# Revit family: Q90.195.xxx_with 3 shelves_4+6 drawers
name_source: partatom
category: Möbelsysteme
revit_build: Autodesk Revit 2016 (Build: 20161004_0715(x64)
units: mm (PartAtom-declared; Revit-internal decimal feet)

## family parameters
Arbeitsebenenbasiert = Nein
Beim Laden mit Abzugskörper schneiden = Nein
Bemaßung runder Anschluss = Durchmesser verwenden
Gemeinsam genutzt = Nein
Immer vertikal = Ja
OmniClass-Nummer = 23.40.70.11.11.11.34
OmniClass-Titel = Laboratory Flammables Storage Cabinets
Raumberechnungspunkt = Nein
Teiletyp = Normal

## types (27) — shared parameters
Beschreibung = GS-tested safety storage cabinets for unrestricted storage of flammable hazardous materials in work areas in accordance with EN 14470-1 and TRGS 510 with a fire resistance of 90 (Type 90)
Diff. pressure (Air change 10 times) = 5.0 Pa
Hersteller = asecos GmbH
Price information = Price from fall 2017
Product video = https://www.youtube.com
Sticker position = 13 mm
URL = https://www.asecos.com
cabinet depth = 617 mm
cabinet height = 1968 mm  [stored 6.45669 ft]

## per-type parameters (varying)
- S90.196.060(.WDAS) with 3 shelves, light grey: 1200 mm 3 shelves=Nein; 1200 mm 4 drawers=Nein; 1200 mm 6 drawers=Nein; 600 mm 3 shelves=Ja; 600 mm 4 drawers=Nein; 600 mm 6 drawers=Nein; 600 mm cabinet=Ja; 900 mm 3 shelves=Nein; 900 mm 4 drawers=Nein; 900 mm 6 drawers=Nein; 900/1200 mm cabinet=Nein; Air change 10 times=1.1 L/s; Bestellnummer DACH=30228-001-30249; Distributed load=893.00 kg/m²; Kosten=2300 $; Modell=S90.196.060.WDAS; Order No. Global Markets=30228-001-33659; Price information 2=Prices in EURO, ex works, without taxes and shipping; Typenbild=30227-001.jpg; air duct distance=130 mm  [stored 0.426509 ft]; cabinet colour=RAL 7035 Light grey; cabinet width=597 mm; door width=514 mm  [stored 1.68635 ft]; handle l=500 mm; handle r=507 mm  [stored 1.66339 ft]; handle r visibility=Nein; visibility drill_small=-3 mm; visibility drill_wide=1 mm  [stored 0.00328084 ft]
- S90.196.060(.WDAS) with 4 drawers, light grey: 1200 mm 3 shelves=Nein; 1200 mm 4 drawers=Nein; 1200 mm 6 drawers=Nein; 600 mm 3 shelves=Nein; 600 mm 4 drawers=Ja; 600 mm 6 drawers=Nein; 600 mm cabinet=Ja; 900 mm 3 shelves=Nein; 900 mm 4 drawers=Nein; 900 mm 6 drawers=Nein; 900/1200 mm cabinet=Nein; Air change 10 times=1.1 L/s; Bestellnummer DACH=30228-001-30267; Distributed load=893.00 kg/m²; Kosten=2610 $; Modell=S90.196.060.WDAS; Order No. Global Markets=30228-001-33681; Price information 2=Prices are ex works and without taxes and shipping; Typenbild=30227-001.jpg; air duct distance=130 mm  [stored 0.426509 ft]; cabinet colour=RAL 7035 Light grey; cabinet width=597 mm; door width=514 mm  [stored 1.68635 ft]; handle l=500 mm; handle r=507 mm  [stored 1.66339 ft]; handle r visibility=Nein; visibility drill_small=-3 mm; visibility drill_wide=1 mm  [stored 0.00328084 ft]
- S90.196.060(.WDAS) with 6 drawers, light grey: 1200 mm 3 shelves=Nein; 1200 mm 4 drawers=Nein; 1200 mm 6 drawers=Nein; 600 mm 3 shelves=Nein; 600 mm 4 drawers=Nein; 600 mm 6 drawers=Ja; 600 mm cabinet=Ja; 900 mm 3 shelves=Nein; 900 mm 4 drawers=Nein; 900 mm 6 drawers=Nein; 900/1200 mm cabinet=Nein; Air change 10 times=1.1 L/s; Bestellnummer DACH=30228-001-30269; Distributed load=893.00 kg/m²; Kosten=2850 $; Modell=S90.196.060.WDAS; Order No. Global Markets=30228-001-33683; Price information 2=Prices are ex works and without taxes and shipping; Typenbild=30227-001.jpg; air duct distance=130 mm  [stored 0.426509 ft]; cabinet colour=RAL 7035 Light grey; cabinet width=597 mm; door width=514 mm  [stored 1.68635 ft]; handle l=500 mm; handle r=507 mm  [stored 1.66339 ft]; handle r visibility=Nein; visibility drill_small=-3 mm; visibility drill_wide=1 mm  [stored 0.00328084 ft]
- S90.196.060(.WDAS) with 3 shelves, warning yellow: 1200 mm 3 shelves=Nein; 1200 mm 4 drawers=Nein; 1200 mm 6 drawers=Nein; 600 mm 3 shelves=Ja; 600 mm 4 drawers=Nein; 600 mm 6 drawers=Nein; 600 mm cabinet=Ja; 900 mm 3 shelves=Nein; 900 mm 4 drawers=Nein; 900 mm 6 drawers=Nein; 900/1200 mm cabinet=Nein; Air change 10 times=1.1 L/s; Bestellnummer DACH=30228-002-30249; Distributed load=893.00 kg/m²; Kosten=2300 $; Modell=S90.196.060.WDAS; Order No. Global Markets=30228-002-33659; Price information 2=Prices are ex works and without taxes and shipping; Typenbild=30227-002.jpg; air duct distance=130 mm  [stored 0.426509 ft]; cabinet colour=RAL 1004 Warning yellow; cabinet width=597 mm; door width=514 mm  [stored 1.68635 ft]; handle l=500 mm; handle r=507 mm  [stored 1.66339 ft]; handle r visibility=Nein; visibility drill_small=-3 mm; visibility drill_wide=1 mm  [stored 0.00328084 ft]
- S90.196.060(.WDAS) with 4 drawers, warning yellow: 1200 mm 3 shelves=Nein; 1200 mm 4 drawers=Nein; 1200 mm 6 drawers=Nein; 600 mm 3 shelves=Nein; 600 mm 4 drawers=Ja; 600 mm 6 drawers=Nein; 600 mm cabinet=Ja; 900 mm 3 shelves=Nein; 900 mm 4 drawers=Nein; 900 mm 6 drawers=Nein; 900/1200 mm cabinet=Nein; Air change 10 times=1.1 L/s; Bestellnummer DACH=30228-002-30267; Distributed load=893.00 kg/m²; Kosten=2610 $; Modell=S90.196.060.WDAS; Order No. Global Markets=30228-002-33681; Price information 2=Prices are ex works and without taxes and shipping; Typenbild=30227-002.jpg; air duct distance=130 mm  [stored 0.426509 ft]; cabinet colour=RAL 1004 Warning yellow; cabinet width=597 mm; door width=514 mm  [stored 1.68635 ft]; handle l=500 mm; handle r=507 mm  [stored 1.66339 ft]; handle r visibility=Nein; visibility drill_small=-3 mm; visibility drill_wide=1 mm  [stored 0.00328084 ft]
- S90.196.060(.WDAS) with 6 drawers, warning yellow: 1200 mm 3 shelves=Nein; 1200 mm 4 drawers=Nein; 1200 mm 6 drawers=Nein; 600 mm 3 shelves=Nein; 600 mm 4 drawers=Nein; 600 mm 6 drawers=Ja; 600 mm cabinet=Ja; 900 mm 3 shelves=Nein; 900 mm 4 drawers=Nein; 900 mm 6 drawers=Nein; 900/1200 mm cabinet=Nein; Air change 10 times=1.1 L/s; Bestellnummer DACH=30228-002-30269; Distributed load=893.00 kg/m²; Kosten=2850 $; Modell=S90.196.060.WDAS; Order No. Global Markets=30228-002-33683; Price information 2=Prices are ex works and without taxes and shipping; Typenbild=30227-002.jpg; air duct distance=130 mm  [stored 0.426509 ft]; cabinet colour=RAL 1004 Warning yellow; cabinet width=597 mm; door width=514 mm  [stored 1.68635 ft]; handle l=500 mm; handle r=507 mm  [stored 1.66339 ft]; handle r visibility=Nein; visibility drill_small=-3 mm; visibility drill_wide=1 mm  [stored 0.00328084 ft]
- S90.196.090(.WDAS) with 3 shelves, light grey: 1200 mm 3 shelves=Nein; 1200 mm 4 drawers=Nein; 1200 mm 6 drawers=Nein; 600 mm 3 shelves=Nein; 600 mm 4 drawers=Nein; 600 mm 6 drawers=Nein; 600 mm cabinet=Nein; 900 mm 3 shelves=Ja; 900 mm 4 drawers=Nein; 900 mm 6 drawers=Nein; 900/1200 mm cabinet=Ja; Air change 10 times=1.9 L/s; Bestellnummer DACH=30205-001-30208; Distributed load=628.00 kg/m²; Kosten=2860 $; Modell=S90.196.090.WDAS; Order No. Global Markets=30205-001-33705; Price information 2=Prices are ex works and without taxes and shipping; Typenbild=30204-001.jpg; air duct distance=115 mm  [stored 0.377297 ft]; cabinet colour=RAL 7035 Light grey; cabinet width=897 mm; door width=403 mm; handle l=389 mm; handle r=507 mm  [stored 1.66339 ft]; handle r visibility=Ja; visibility drill_small=1 mm  [stored 0.00328084 ft]; visibility drill_wide=-3 mm
- S90.196.090(.WDAS) with 4 drawers, light grey: 1200 mm 3 shelves=Nein; 1200 mm 4 drawers=Nein; 1200 mm 6 drawers=Nein; 600 mm 3 shelves=Nein; 600 mm 4 drawers=Nein; 600 mm 6 drawers=Nein; 600 mm cabinet=Nein; 900 mm 3 shelves=Nein; 900 mm 4 drawers=Ja; 900 mm 6 drawers=Nein; 900/1200 mm cabinet=Ja; Air change 10 times=1.9 L/s; Bestellnummer DACH=30205-001-30218; Distributed load=628.00 kg/m²; Kosten=3420 $; Modell=S90.196.090.WDAS; Order No. Global Markets=30205-001-33709; Price information 2=Prices are ex works and without taxes and shipping; Typenbild=30204-001.jpg; air duct distance=115 mm  [stored 0.377297 ft]; cabinet colour=RAL 7035 Light grey; cabinet width=897 mm; door width=403 mm; handle l=389 mm; handle r=507 mm  [stored 1.66339 ft]; handle r visibility=Ja; visibility drill_small=1 mm  [stored 0.00328084 ft]; visibility drill_wide=-3 mm
- S90.196.090(.WDAS) with 6 drawers, light grey: 1200 mm 3 shelves=Nein; 1200 mm 4 drawers=Nein; 1200 mm 6 drawers=Nein; 600 mm 3 shelves=Nein; 600 mm 4 drawers=Nein; 600 mm 6 drawers=Nein; 600 mm cabinet=Nein; 900 mm 3 shelves=Nein; 900 mm 4 drawers=Nein; 900 mm 6 drawers=Ja; 900/1200 mm cabinet=Ja; Air change 10 times=1.9 L/s; Bestellnummer DACH=30205-001-30220; Distributed load=628.00 kg/m²; Kosten=3800 $; Modell=S90.196.090.WDAS; Order No. Global Markets=30205-001-33711; Price information 2=Prices are ex works and without taxes and shipping; Typenbild=30204-001.jpg; air duct distance=115 mm  [stored 0.377297 ft]; cabinet colour=RAL 7035 Light grey; cabinet width=897 mm; door width=403 mm; handle l=389 mm; handle r=507 mm  [stored 1.66339 ft]; handle r visibility=Ja; visibility drill_small=1 mm  [stored 0.00328084 ft]; visibility drill_wide=-3 mm
- S90.196.090(.WDAS) with 3 shelves, warning yellow: 1200 mm 3 shelves=Nein; 1200 mm 4 drawers=Nein; 1200 mm 6 drawers=Nein; 600 mm 3 shelves=Nein; 600 mm 4 drawers=Nein; 600 mm 6 drawers=Nein; 600 mm cabinet=Nein; 900 mm 3 shelves=Ja; 900 mm 4 drawers=Nein; 900 mm 6 drawers=Nein; 900/1200 mm cabinet=Ja; Air change 10 times=1.9 L/s; Bestellnummer DACH=30205-002-30208; Distributed load=628.00 kg/m²; Kosten=2860 $; Modell=S90.196.090.WDAS; Order No. Global Markets=30205-002-33705; Price information 2=Prices are ex works and without taxes and shipping; Typenbild=30204-002.jpg; air duct distance=115 mm  [stored 0.377297 ft]; cabinet colour=RAL 1004 Warning yellow; cabinet width=897 mm; door width=403 mm; handle l=389 mm; handle r=507 mm  [stored 1.66339 ft]; handle r visibility=Ja; visibility drill_small=1 mm  [stored 0.00328084 ft]; visibility drill_wide=-3 mm
- S90.196.090(.WDAS) with 4 drawers, warning yellow: 1200 mm 3 shelves=Nein; 1200 mm 4 drawers=Nein; 1200 mm 6 drawers=Nein; 600 mm 3 shelves=Nein; 600 mm 4 drawers=Nein; 600 mm 6 drawers=Nein; 600 mm cabinet=Nein; 900 mm 3 shelves=Nein; 900 mm 4 drawers=Ja; 900 mm 6 drawers=Nein; 900/1200 mm cabinet=Ja; Air change 10 times=1.9 L/s; Bestellnummer DACH=30205-002-30218; Distributed load=628.00 kg/m²; Kosten=3420 $; Modell=S90.196.090.WDAS; Order No. Global Markets=30205-002-33709; Price information 2=Prices are ex works and without taxes and shipping; Typenbild=30204-002.jpg; air duct distance=115 mm  [stored 0.377297 ft]; cabinet colour=RAL 1004 Warning yellow; cabinet width=897 mm; door width=403 mm; handle l=389 mm; handle r=507 mm  [stored 1.66339 ft]; handle r visibility=Ja; visibility drill_small=1 mm  [stored 0.00328084 ft]; visibility drill_wide=-3 mm
- S90.196.090(.WDAS) with 6 drawers, warning yellow: 1200 mm 3 shelves=Nein; 1200 mm 4 drawers=Nein; 1200 mm 6 drawers=Nein; 600 mm 3 shelves=Nein; 600 mm 4 drawers=Nein; 600 mm 6 drawers=Nein; 600 mm cabinet=Nein; 900 mm 3 shelves=Nein; 900 mm 4 drawers=Nein; 900 mm 6 drawers=Ja; 900/1200 mm cabinet=Ja; Air change 10 times=1.9 L/s; Bestellnummer DACH=30205-002-30220; Distributed load=628.00 kg/m²; Kosten=3800 $; Modell=S90.196.090.WDAS; Order No. Global Markets=30205-002-33711; Price information 2=Prices are ex works and without taxes and shipping; Typenbild=30204-002.jpg; air duct distance=115 mm  [stored 0.377297 ft]; cabinet colour=RAL 1004 Warning yellow; cabinet width=897 mm; door width=403 mm; handle l=389 mm; handle r=507 mm  [stored 1.66339 ft]; handle r visibility=Ja; visibility drill_small=1 mm  [stored 0.00328084 ft]; visibility drill_wide=-3 mm
- S90.196.120(.WDAS) with 3 shelves, light grey: 1200 mm 3 shelves=Ja; 1200 mm 4 drawers=Nein; 1200 mm 6 drawers=Nein; 600 mm 3 shelves=Nein; 600 mm 4 drawers=Nein; 600 mm 6 drawers=Nein; 600 mm cabinet=Nein; 900 mm 3 shelves=Nein; 900 mm 4 drawers=Nein; 900 mm 6 drawers=Nein; 900/1200 mm cabinet=Ja; Air change 10 times=2.8 L/s; Bestellnummer DACH=30116-001-30127; Distributed load=528.00 kg/m²; Kosten=2970 $; Modell=S90.196.120.WDAS; Order No. Global Markets=30116-001-33715; Price information 2=Prices are ex works and without taxes and shipping; Typenbild=30115-001.jpg; air duct distance=115 mm  [stored 0.377297 ft]; cabinet colour=RAL 7035 Light grey; cabinet width=1197 mm; door width=553 mm; handle l=538 mm; handle r=658 mm; handle r visibility=Ja; visibility drill_small=1 mm  [stored 0.00328084 ft]; visibility drill_wide=-3 mm
- S90.196.120(.WDAS) with 4 drawers, light grey: 1200 mm 3 shelves=Nein; 1200 mm 4 drawers=Ja; 1200 mm 6 drawers=Nein; 600 mm 3 shelves=Nein; 600 mm 4 drawers=Nein; 600 mm 6 drawers=Nein; 600 mm cabinet=Nein; 900 mm 3 shelves=Nein; 900 mm 4 drawers=Nein; 900 mm 6 drawers=Nein; 900/1200 mm cabinet=Ja; Air change 10 times=2.8 L/s; Bestellnummer DACH=30116-001-30147; Distributed load=528.00 kg/m²; Kosten=3530 $; Modell=S90.196.120.WDAS; Order No. Global Markets=30116-001-33724; Price information 2=Prices are ex works and without taxes and shipping; Typenbild=30115-001.jpg; air duct distance=115 mm  [stored 0.377297 ft]; cabinet colour=RAL 7035 Light grey; cabinet width=1197 mm; door width=553 mm; handle l=538 mm; handle r=658 mm; handle r visibility=Ja; visibility drill_small=1 mm  [stored 0.00328084 ft]; visibility drill_wide=-3 mm
- S90.196.120(.WDAS) with 6 drawers, light grey: 1200 mm 3 shelves=Nein; 1200 mm 4 drawers=Nein; 1200 mm 6 drawers=Ja; 600 mm 3 shelves=Nein; 600 mm 4 drawers=Nein; 600 mm 6 drawers=Nein; 600 mm cabinet=Nein; 900 mm 3 shelves=Nein; 900 mm 4 drawers=Nein; 900 mm 6 drawers=Nein; 900/1200 mm cabinet=Ja; Air change 10 times=2.8 L/s; Bestellnummer DACH=30116-001-30149; Distributed load=528.00 kg/m²; Kosten=3910 $; Modell=S90.196.120.WDAS; Order No. Global Markets=30116-001-33726; Price information 2=Prices are ex works and without taxes and shipping; Typenbild=30115-001.jpg; air duct distance=115 mm  [stored 0.377297 ft]; cabinet colour=RAL 7035 Light grey; cabinet width=1197 mm; door width=553 mm; handle l=538 mm; handle r=658 mm; handle r visibility=Ja; visibility drill_small=1 mm  [stored 0.00328084 ft]; visibility drill_wide=-3 mm
- S90.196.120(.WDAS) with 3 shelves, warning yellow: 1200 mm 3 shelves=Ja; 1200 mm 4 drawers=Nein; 1200 mm 6 drawers=Nein; 600 mm 3 shelves=Nein; 600 mm 4 drawers=Nein; 600 mm 6 drawers=Nein; 600 mm cabinet=Nein; 900 mm 3 shelves=Nein; 900 mm 4 drawers=Nein; 900 mm 6 drawers=Nein; 900/1200 mm cabinet=Ja; Air change 10 times=2.8 L/s; Bestellnummer DACH=30116-002-30127; Distributed load=528.00 kg/m²; Kosten=2970 $; Modell=S90.196.120.WDAS; Order No. Global Markets=30116-002-33715; Price information 2=Prices are ex works and without taxes and shipping; Typenbild=30115-002.jpg; air duct distance=115 mm  [stored 0.377297 ft]; cabinet colour=RAL 1004 Warning yellow; cabinet width=1197 mm; door width=553 mm; handle l=538 mm; handle r=658 mm; handle r visibility=Ja; visibility drill_small=1 mm  [stored 0.00328084 ft]; visibility drill_wide=-3 mm
- S90.196.120(.WDAS) with 4 drawers, warning yellow: 1200 mm 3 shelves=Nein; 1200 mm 4 drawers=Ja; 1200 mm 6 drawers=Nein; 600 mm 3 shelves=Nein; 600 mm 4 drawers=Nein; 600 mm 6 drawers=Nein; 600 mm cabinet=Nein; 900 mm 3 shelves=Nein; 900 mm 4 drawers=Nein; 900 mm 6 drawers=Nein; 900/1200 mm cabinet=Ja; Air change 10 times=2.8 L/s; Bestellnummer DACH=30116-002-30147; Distributed load=528.00 kg/m²; Kosten=3530 $; Modell=S90.196.120.WDAS; Order No. Global Markets=30116-002-33724; Price information 2=Prices are ex works and without taxes and shipping; Typenbild=30115-002.jpg; air duct distance=115 mm  [stored 0.377297 ft]; cabinet colour=RAL 1004 Warning yellow; cabinet width=1197 mm; door width=553 mm; handle l=538 mm; handle r=658 mm; handle r visibility=Ja; visibility drill_small=1 mm  [stored 0.00328084 ft]; visibility drill_wide=-3 mm
- S90.196.120(.WDAS) with 6 drawers, warning yellow: 1200 mm 3 shelves=Nein; 1200 mm 4 drawers=Nein; 1200 mm 6 drawers=Ja; 600 mm 3 shelves=Nein; 600 mm 4 drawers=Nein; 600 mm 6 drawers=Nein; 600 mm cabinet=Nein; 900 mm 3 shelves=Nein; 900 mm 4 drawers=Nein; 900 mm 6 drawers=Nein; 900/1200 mm cabinet=Ja; Air change 10 times=2.8 L/s; Bestellnummer DACH=30116-002-30149; Distributed load=528.00 kg/m²; Kosten=3910 $; Modell=S90.196.120.WDAS; Order No. Global Markets=30116-002-33726; Price information 2=Prices are ex works and without taxes and shipping; Typenbild=30115-002.jpg; air duct distance=115 mm  [stored 0.377297 ft]; cabinet colour=RAL 1004 Warning yellow; cabinet width=1197 mm; door width=553 mm; handle l=538 mm; handle r=658 mm; handle r visibility=Ja; visibility drill_small=1 mm  [stored 0.00328084 ft]; visibility drill_wide=-3 mm
- S90.196.060(.WDAS) with 3 shelves, pure white: 1200 mm 3 shelves=Nein; 1200 mm 4 drawers=Nein; 1200 mm 6 drawers=Nein; 600 mm 3 shelves=Ja; 600 mm 4 drawers=Nein; 600 mm 6 drawers=Nein; 600 mm cabinet=Ja; 900 mm 3 shelves=Nein; 900 mm 4 drawers=Nein; 900 mm 6 drawers=Nein; 900/1200 mm cabinet=Nein; Air change 10 times=1.1 L/s; Bestellnummer DACH=30228-001-30249; Distributed load=893.00 kg/m²; Kosten=2300 $; Modell=S90.196.060.WDAS; Order No. Global Markets=30228-001-33659; Price information 2=Prices in EURO, ex works, without taxes and shipping; Typenbild=30227-001.jpg; air duct distance=130 mm  [stored 0.426509 ft]; cabinet colour=RAL 9010 Pure white; cabinet width=597 mm; door width=514 mm  [stored 1.68635 ft]; handle l=500 mm; handle r=507 mm  [stored 1.66339 ft]; handle r visibility=Nein; visibility drill_small=-3 mm; visibility drill_wide=1 mm  [stored 0.00328084 ft]
- S90.196.060(.WDAS) with 4 drawers, pure white: 1200 mm 3 shelves=Nein; 1200 mm 4 drawers=Nein; 1200 mm 6 drawers=Nein; 600 mm 3 shelves=Nein; 600 mm 4 drawers=Ja; 600 mm 6 drawers=Nein; 600 mm cabinet=Ja; 900 mm 3 shelves=Nein; 900 mm 4 drawers=Nein; 900 mm 6 drawers=Nein; 900/1200 mm cabinet=Nein; Air change 10 times=1.1 L/s; Bestellnummer DACH=30228-001-30267; Distributed load=893.00 kg/m²; Kosten=2610 $; Modell=S90.196.060.WDAS; Order No. Global Markets=30228-001-33681; Price information 2=Prices are ex works and without taxes and shipping; Typenbild=30227-001.jpg; air duct distance=130 mm  [stored 0.426509 ft]; cabinet colour=RAL 9010 Pure white; cabinet width=597 mm; door width=514 mm  [stored 1.68635 ft]; handle l=500 mm; handle r=507 mm  [stored 1.66339 ft]; handle r visibility=Nein; visibility drill_small=-3 mm; visibility drill_wide=1 mm  [stored 0.00328084 ft]
- S90.196.060(.WDAS) with 6 drawers, pure white: 1200 mm 3 shelves=Nein; 1200 mm 4 drawers=Nein; 1200 mm 6 drawers=Nein; 600 mm 3 shelves=Nein; 600 mm 4 drawers=Nein; 600 mm 6 drawers=Ja; 600 mm cabinet=Ja; 900 mm 3 shelves=Nein; 900 mm 4 drawers=Nein; 900 mm 6 drawers=Nein; 900/1200 mm cabinet=Nein; Air change 10 times=1.1 L/s; Bestellnummer DACH=30228-001-30269; Distributed load=893.00 kg/m²; Kosten=2850 $; Modell=S90.196.060.WDAS; Order No. Global Markets=30228-001-33683; Price information 2=Prices are ex works and without taxes and shipping; Typenbild=30227-001.jpg; air duct distance=130 mm  [stored 0.426509 ft]; cabinet colour=RAL 9010 Pure white; cabinet width=597 mm; door width=514 mm  [stored 1.68635 ft]; handle l=500 mm; handle r=507 mm  [stored 1.66339 ft]; handle r visibility=Nein; visibility drill_small=-3 mm; visibility drill_wide=1 mm  [stored 0.00328084 ft]
- S90.196.090(.WDAS) with 3 shelves, pure white: 1200 mm 3 shelves=Nein; 1200 mm 4 drawers=Nein; 1200 mm 6 drawers=Nein; 600 mm 3 shelves=Nein; 600 mm 4 drawers=Nein; 600 mm 6 drawers=Nein; 600 mm cabinet=Nein; 900 mm 3 shelves=Ja; 900 mm 4 drawers=Nein; 900 mm 6 drawers=Nein; 900/1200 mm cabinet=Ja; Air change 10 times=1.9 L/s; Bestellnummer DACH=30205-001-30208; Distributed load=628.00 kg/m²; Kosten=2860 $; Modell=S90.196.090.WDAS; Order No. Global Markets=30205-001-33705; Price information 2=Prices are ex works and without taxes and shipping; Typenbild=30204-001.jpg; air duct distance=115 mm  [stored 0.377297 ft]; cabinet colour=RAL 9010 Pure white; cabinet width=897 mm; door width=403 mm; handle l=389 mm; handle r=507 mm  [stored 1.66339 ft]; handle r visibility=Ja; visibility drill_small=1 mm  [stored 0.00328084 ft]; visibility drill_wide=-3 mm
- S90.196.090(.WDAS) with 4 drawers, pure white: 1200 mm 3 shelves=Nein; 1200 mm 4 drawers=Nein; 1200 mm 6 drawers=Nein; 600 mm 3 shelves=Nein; 600 mm 4 drawers=Nein; 600 mm 6 drawers=Nein; 600 mm cabinet=Nein; 900 mm 3 shelves=Nein; 900 mm 4 drawers=Ja; 900 mm 6 drawers=Nein; 900/1200 mm cabinet=Ja; Air change 10 times=1.9 L/s; Bestellnummer DACH=30205-001-30218; Distributed load=628.00 kg/m²; Kosten=3420 $; Modell=S90.196.090.WDAS; Order No. Global Markets=30205-001-33709; Price information 2=Prices are ex works and without taxes and shipping; Typenbild=30204-001.jpg; air duct distance=115 mm  [stored 0.377297 ft]; cabinet colour=RAL 9010 Pure white; cabinet width=897 mm; door width=403 mm; handle l=389 mm; handle r=507 mm  [stored 1.66339 ft]; handle r visibility=Ja; visibility drill_small=1 mm  [stored 0.00328084 ft]; visibility drill_wide=-3 mm
- S90.196.090(.WDAS) with 6 drawers, pure white: 1200 mm 3 shelves=Nein; 1200 mm 4 drawers=Nein; 1200 mm 6 drawers=Nein; 600 mm 3 shelves=Nein; 600 mm 4 drawers=Nein; 600 mm 6 drawers=Nein; 600 mm cabinet=Nein; 900 mm 3 shelves=Nein; 900 mm 4 drawers=Nein; 900 mm 6 drawers=Ja; 900/1200 mm cabinet=Ja; Air change 10 times=1.9 L/s; Bestellnummer DACH=30205-001-30220; Distributed load=628.00 kg/m²; Kosten=3800 $; Modell=S90.196.090.WDAS; Order No. Global Markets=30205-001-33711; Price information 2=Prices are ex works and without taxes and shipping; Typenbild=30204-001.jpg; air duct distance=115 mm  [stored 0.377297 ft]; cabinet colour=RAL 9010 Pure white; cabinet width=897 mm; door width=403 mm; handle l=389 mm; handle r=507 mm  [stored 1.66339 ft]; handle r visibility=Ja; visibility drill_small=1 mm  [stored 0.00328084 ft]; visibility drill_wide=-3 mm
- S90.196.120(.WDAS) with 3 shelves, pure white: 1200 mm 3 shelves=Ja; 1200 mm 4 drawers=Nein; 1200 mm 6 drawers=Nein; 600 mm 3 shelves=Nein; 600 mm 4 drawers=Nein; 600 mm 6 drawers=Nein; 600 mm cabinet=Nein; 900 mm 3 shelves=Nein; 900 mm 4 drawers=Nein; 900 mm 6 drawers=Nein; 900/1200 mm cabinet=Ja; Air change 10 times=2.8 L/s; Bestellnummer DACH=30116-001-30127; Distributed load=528.00 kg/m²; Kosten=2970 $; Modell=S90.196.120.WDAS; Order No. Global Markets=30116-001-33715; Price information 2=Prices are ex works and without taxes and shipping; Typenbild=30115-001.jpg; air duct distance=115 mm  [stored 0.377297 ft]; cabinet colour=RAL 9010 Pure white; cabinet width=1197 mm; door width=553 mm; handle l=538 mm; handle r=658 mm; handle r visibility=Ja; visibility drill_small=1 mm  [stored 0.00328084 ft]; visibility drill_wide=-3 mm
- S90.196.120(.WDAS) with 4 drawers, pure white: 1200 mm 3 shelves=Nein; 1200 mm 4 drawers=Ja; 1200 mm 6 drawers=Nein; 600 mm 3 shelves=Nein; 600 mm 4 drawers=Nein; 600 mm 6 drawers=Nein; 600 mm cabinet=Nein; 900 mm 3 shelves=Nein; 900 mm 4 drawers=Nein; 900 mm 6 drawers=Nein; 900/1200 mm cabinet=Ja; Air change 10 times=2.8 L/s; Bestellnummer DACH=30116-001-30147; Distributed load=528.00 kg/m²; Kosten=3530 $; Modell=S90.196.120.WDAS; Order No. Global Markets=30116-001-33724; Price information 2=Prices are ex works and without taxes and shipping; Typenbild=30115-001.jpg; air duct distance=115 mm  [stored 0.377297 ft]; cabinet colour=RAL 9010 Pure white; cabinet width=1197 mm; door width=553 mm; handle l=538 mm; handle r=658 mm; handle r visibility=Ja; visibility drill_small=1 mm  [stored 0.00328084 ft]; visibility drill_wide=-3 mm
- S90.196.120(.WDAS) with 6 drawers, pure white: 1200 mm 3 shelves=Nein; 1200 mm 4 drawers=Nein; 1200 mm 6 drawers=Ja; 600 mm 3 shelves=Nein; 600 mm 4 drawers=Nein; 600 mm 6 drawers=Nein; 600 mm cabinet=Nein; 900 mm 3 shelves=Nein; 900 mm 4 drawers=Nein; 900 mm 6 drawers=Nein; 900/1200 mm cabinet=Ja; Air change 10 times=2.8 L/s; Bestellnummer DACH=30116-001-30149; Distributed load=528.00 kg/m²; Kosten=3910 $; Modell=S90.196.120.WDAS; Order No. Global Markets=30116-001-33726; Price information 2=Prices are ex works and without taxes and shipping; Typenbild=30115-001.jpg; air duct distance=115 mm  [stored 0.377297 ft]; cabinet colour=RAL 9010 Pure white; cabinet width=1197 mm; door width=553 mm; handle l=538 mm; handle r=658 mm; handle r visibility=Ja; visibility drill_small=1 mm  [stored 0.00328084 ft]; visibility drill_wide=-3 mm

note: [stored X ft] marks values corroborated as IEEE doubles in the binary element streams (Revit-internal decimal feet)
